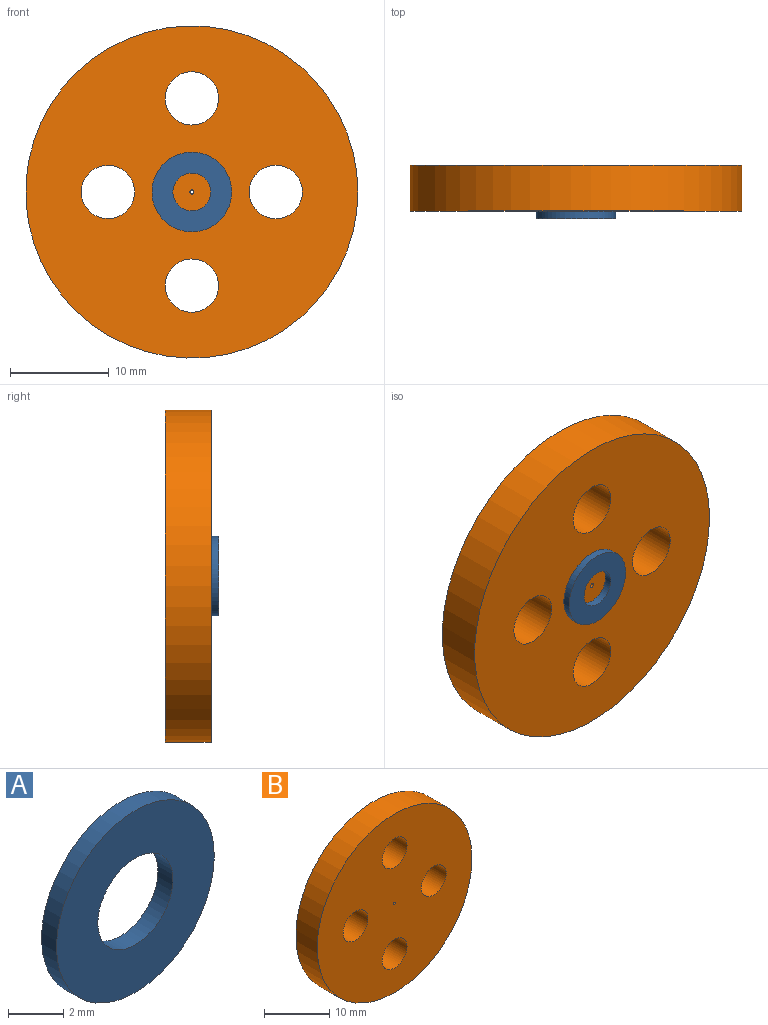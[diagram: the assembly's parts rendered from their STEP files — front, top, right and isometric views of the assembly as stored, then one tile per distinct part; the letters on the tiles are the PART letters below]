
ASSEMBLY  parts=2 mates=1
PART A: 4 faces, bbox 8.1x0.8x8.1 mm
  f0: cylinder r=1.92mm len=3.84mm, axis (0,1,0), area 9.2mm2, adj f1,f2
  f1: plane 8.05x8.05mm, normal (0,-1,0), area 39.4mm2, adj f0,f3
  f2: plane 8.05x8.05mm, normal (0,1,0), area 39.4mm2, adj f0,f3
  f3: cylinder r=4.03mm len=8.05mm, axis (0,1,0), area 19.3mm2, adj f1,f2
PART B: 8 faces, bbox 33.6x4.6x33.6 mm
  f0: cylinder r=2.69mm len=5.39mm, axis (0,-1,0), area 78.2mm2, adj f5,f6
  f1: cylinder r=2.69mm len=5.39mm, axis (0,-1,0), area 78.2mm2, adj f5,f6
  f2: cylinder r=2.69mm len=5.39mm, axis (0,-1,0), area 78.2mm2, adj f5,f6
  f3: cylinder r=2.69mm len=5.39mm, axis (0,-1,0), area 78.2mm2, adj f5,f6
  f4: cylinder r=0.2mm len=4.62mm, axis (0,-1,0), area 5.9mm2, adj f5,f6
  f5: plane 33.55x33.55mm, normal (0,1,0), area 793mm2, adj f0,f1,f2,f3,f4,f7
  f6: plane 33.55x33.55mm, normal (0,-1,0), area 793mm2, adj f0,f1,f2,f3,f4,f7
  f7: cylinder r=16.78mm len=33.55mm, axis (0,-1,0), area 487.3mm2, adj f5,f6
PLACE A t=(-33.47,1,31.06)mm
PLACE B t=(-33.47,6.38,31.06)mm
MATE revolute B.f4 <-> A.f0  axis (0,-1,0) through (-33.47,1.76,31.06)mm
